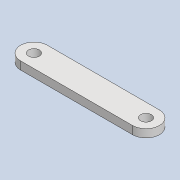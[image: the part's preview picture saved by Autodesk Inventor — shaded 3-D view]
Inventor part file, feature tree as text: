
AUTODESK INVENTOR PART (.ipt)
format: ipt  version: 2022 (Build 260153000, 153)  size: 86,528 bytes
history: native  units: in
note: dims shown in document units (in); Inventor stores cm internally (conversion verified against a paired STEP export)
features: extrude x1, sketch x1
ambient origin geometry x8: Origin, YZ Plane, XZ Plane, XY Plane, X Axis, Y Axis, Z Axis, Center Point
bodies: Solid1 (feature_tree)
feature tree (2):
  extrude  "Extrusion1"  Depth=0.125in
  sketch  "Sketch1"  dims[d0=0.17in d1=0.17in d2=1.75in d3=0.125in d4=0.125in d5=0.125in d6=0.0in]
